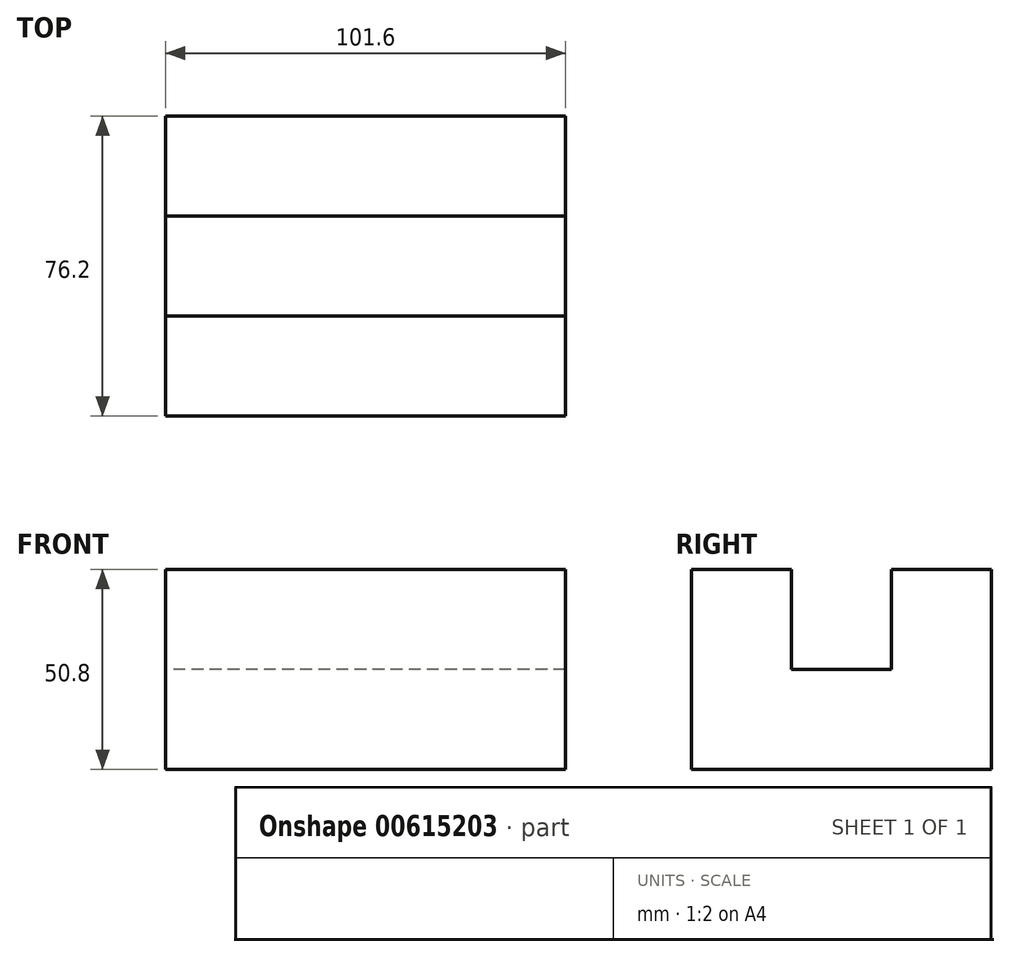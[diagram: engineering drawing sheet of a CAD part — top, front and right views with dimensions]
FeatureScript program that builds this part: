
annotation { "Feature Type Name" : "Feature", "Feature Type Description" : "" }
export const myFeature = defineFeature(function(context is Context, id is Id, definition is map)
    precondition{}
    {
        {
            var Q0;
            Q0=qCreatedBy(makeId("Right.planeOp"),FACE);
            var sketch = newSketch(context, id + "F0", { "sketchPlane" : qUnion([Q0])});
            skLineSegment(sketch, "E0", {"start": v(0, 0) * mm, "end": v(76.2, 0) * mm});
            skLineSegment(sketch, "E1", {"start": v(76.2, 0) * mm, "end": v(76.2, 50.8) * mm});
            skLineSegment(sketch, "E2", {"start": v(76.2, 50.8) * mm, "end": v(50.8, 50.8) * mm});
            skLineSegment(sketch, "E3", {"start": v(50.8, 50.8) * mm, "end": v(50.8, 25.4) * mm});
            skLineSegment(sketch, "E4", {"start": v(50.8, 25.4) * mm, "end": v(25.4, 25.4) * mm});
            skLineSegment(sketch, "E5", {"start": v(25.4, 25.4) * mm, "end": v(25.4, 50.8) * mm});
            skLineSegment(sketch, "E6", {"start": v(25.4, 50.8) * mm, "end": v(0, 50.8) * mm});
            skLineSegment(sketch, "E7", {"start": v(0, 50.8) * mm, "end": v(0, 0) * mm});
            skSolve(sketch);
        }
        {
            var Q0;
            Q0 = qSketchRegion(id + "F0", true);
            extrude(context, id + "F1", {"entities" : qUnion([Q0]), "depth" : 101.6 * mm, "offsetDistance" : 25.4 * mm});
        }
    });
